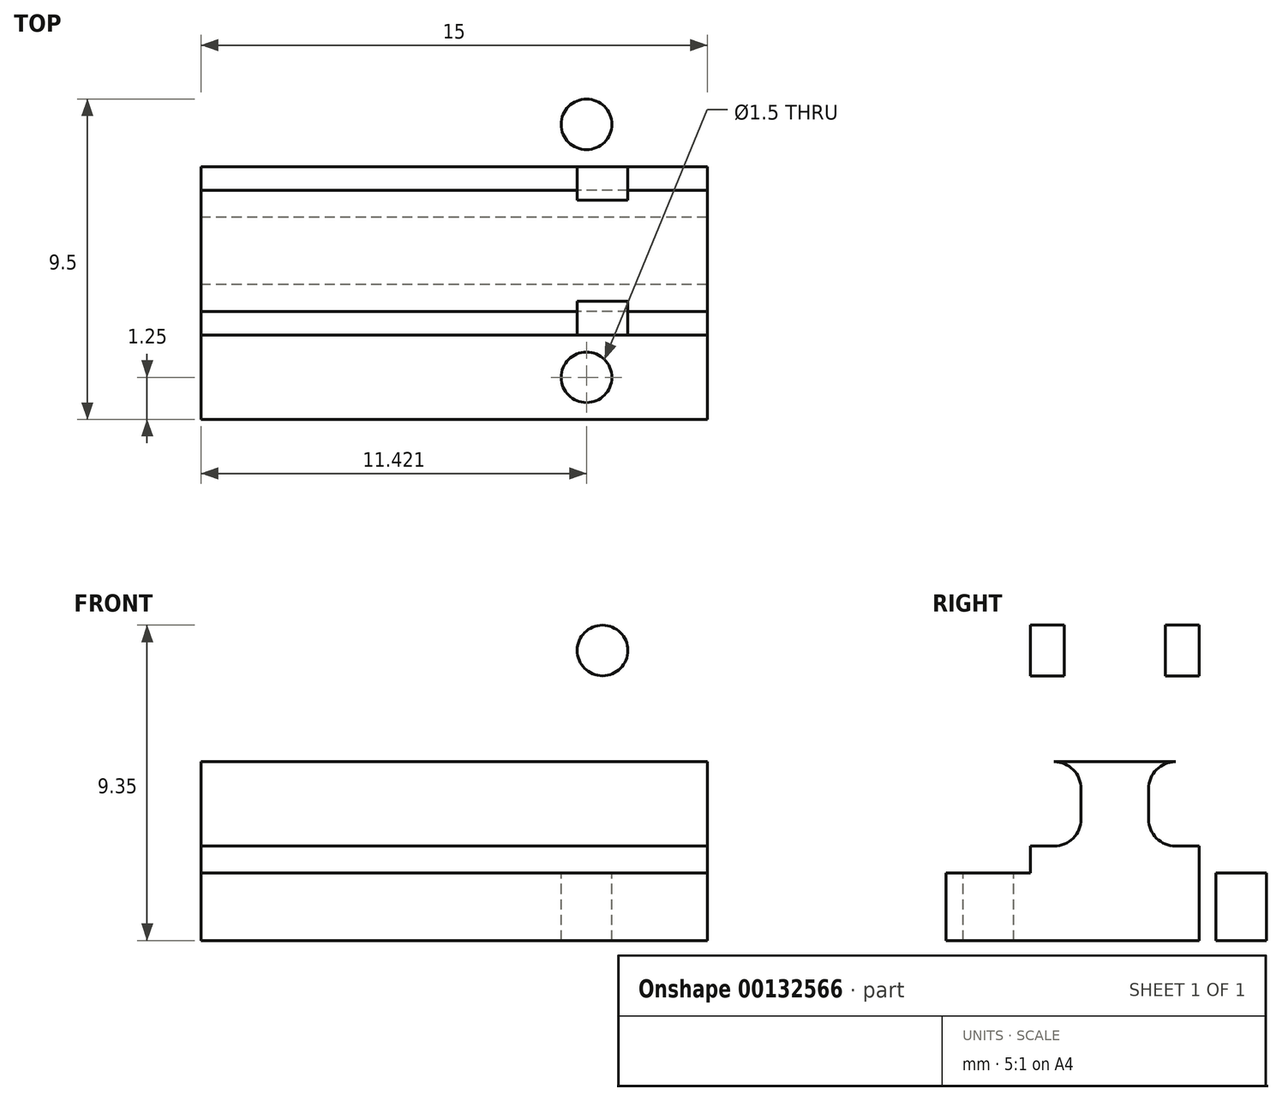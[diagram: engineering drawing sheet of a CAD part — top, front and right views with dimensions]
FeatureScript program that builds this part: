
annotation { "Feature Type Name" : "Feature", "Feature Type Description" : "" }
export const myFeature = defineFeature(function(context is Context, id is Id, definition is map)
    precondition{}
    {
        {
            var Q0;
            Q0=qCreatedBy(makeId("Right.planeOp"),FACE);
            var sketch = newSketch(context, id + "F0", { "sketchPlane" : qUnion([Q0])});
            skLineSegment(sketch, "E0.bottom", {"start": v(-1.5, 2.5) * mm, "end": v(1.5, 2.5) * mm});
            skLineSegment(sketch, "E0.top", {"start": v(-1.5, -2.5) * mm, "end": v(1.5, -2.5) * mm});
            skLineSegment(sketch, "E0.left", {"start": v(-1.5, 2.5) * mm, "end": v(-1.5, -2.5) * mm});
            skLineSegment(sketch, "E0.right", {"start": v(1.5, 2.5) * mm, "end": v(1.5, -2.5) * mm});
            skPoint(sketch, "E0.middle", {"position": v(0, 0) * mm});
            skLineSegment(sketch, "E1.bottom", {"start": v(-2.5, 2.5) * mm, "end": v(2.5, 2.5) * mm});
            skLineSegment(sketch, "E1.left", {"start": v(-2.5, 2.5) * mm, "end": v(-2.5, -7.7) * mm});
            skLineSegment(sketch, "E1.right", {"start": v(2.5, 2.5) * mm, "end": v(2.5, -7.7) * mm});
            skLineSegment(sketch, "E2.bottom", {"start": v(-5, -6.6) * mm, "end": v(5, -6.6) * mm});
            skLineSegment(sketch, "E2.top", {"start": v(-5, -8.6) * mm, "end": v(5, -8.6) * mm});
            skLineSegment(sketch, "E2.left", {"start": v(-5, -6.6) * mm, "end": v(-5, -8.6) * mm});
            skLineSegment(sketch, "E2.right", {"start": v(5, -6.6) * mm, "end": v(5, -8.6) * mm});
            skPoint(sketch, "E2.middle", {"position": v(0, -7.6) * mm});
            skLineSegment(sketch, "E3.bottom", {"start": v(1.8, -3.3) * mm, "end": v(2.5, -3.3) * mm});
            skLineSegment(sketch, "E3.top", {"start": v(1.8, -5.8) * mm, "end": v(2.5, -5.8) * mm});
            skLineSegment(sketch, "E3.left", {"start": v(1, -4.1) * mm, "end": v(1, -5) * mm});
            skLineSegment(sketch, "E3.right", {"start": v(2.5, -3.3) * mm, "end": v(2.5, -5.8) * mm});
            skLineSegment(sketch, "E4.MirrorCS", {"start": v(-1.8, -3.3) * mm, "end": v(-2.5, -3.3) * mm});
            skLineSegment(sketch, "E5.MirrorCS", {"start": v(-1, -4.1) * mm, "end": v(-1, -5) * mm});
            skLineSegment(sketch, "E6.MirrorCS", {"start": v(-1.8, -5.8) * mm, "end": v(-2.5, -5.8) * mm});
            skPoint(sketch, "E7.visualSharp", {"position": v(-1, -3.3) * mm});
            skArc(sketch, "E7.filletArc", {"start": v(-1, -4.1) * mm, "mid": v(-1.23, -3.53) * mm, "end": v(-1.8, -3.3) * mm});
            skPoint(sketch, "E8.visualSharp", {"position": v(-1, -5.8) * mm});
            skArc(sketch, "E8.filletArc", {"start": v(-1.8, -5.8) * mm, "mid": v(-1.23, -5.57) * mm, "end": v(-1, -5) * mm});
            skPoint(sketch, "E9.visualSharp", {"position": v(1, -3.3) * mm});
            skArc(sketch, "E9.filletArc", {"start": v(1.8, -3.3) * mm, "mid": v(1.23, -3.53) * mm, "end": v(1, -4.1) * mm});
            skPoint(sketch, "E10.visualSharp", {"position": v(1, -5.8) * mm});
            skArc(sketch, "E10.filletArc", {"start": v(1, -5) * mm, "mid": v(1.23, -5.57) * mm, "end": v(1.8, -5.8) * mm});
            skSolve(sketch);
        }
        {
            var Q0;
            Q0=makeQuery(id+"F0.imprint","IMPRINT",FACE,{"disambiguationData":[TD([[makeQuery(id+"F0.imprint","IMPRINT",EDGE,{"derivedFrom":sQuery(id+"F0.wireOp",EDGE,"E0.top")}),-1.0]])]});
            var Q1;
            Q1=makeQuery(id+"F0.imprint","IMPRINT",FACE,{"disambiguationData":[TD([[makeQuery(id+"F0.imprint","IMPRINT",EDGE,{"derivedFrom":sQuery(id+"F0.wireOp",EDGE,"E2.top")}),1.0]])]});
            extrude(context, id + "F1", {"entities" : qUnion([Q0, Q1]), "endBound" : BoundingType.SYMMETRIC, "depth" : 15 * mm});
        }
        {
            var Q0;
            {var subQ0=sQuery(id+"F0.wireOp",EDGE,"E1.right");Q0=makeQuery(id+"F1.opExtrude","SWEPT_FACE",FACE,{"disambiguationData":[OSD([subQ0]),TDD([makeQuery(id+"F0.imprint","IMPRINT",EDGE,{"disambiguationData":[TD([[makeQuery(id+"F0.imprint","INTERSECT",VERTEX,{"derivedFrom":[sQuery(id+"F0.wireOp",EDGE,"E1.bottom"),subQ0]}),-1.0]])],"derivedFrom":subQ0})])]});}
            var sketch = newSketch(context, id + "F2", { "sketchPlane" : qUnion([Q0])});
            skCircle(sketch, "E11", {"center": v(4.4, 0) * mm, "radius": 0.75 * mm});
            skCircle(sketch, "E12.MirrorC", {"center": v(-4.4, 0) * mm, "radius": 0.75 * mm});
            skSolve(sketch);
        }
        {
            var Q0;
            Q0=makeQuery(id+"F2.imprint","IMPRINT",FACE,{"disambiguationData":[TD([[makeQuery(id+"F2.imprint","IMPRINT",EDGE,{"derivedFrom":sQuery(id+"F2.wireOp",EDGE,"E12.MirrorC")}),-1.0]])]});
            var Q1;
            Q1=makeQuery(id+"F2.imprint","IMPRINT",FACE,{"disambiguationData":[TD([[makeQuery(id+"F2.imprint","IMPRINT",EDGE,{"derivedFrom":sQuery(id+"F2.wireOp",EDGE,"E11")}),1.0]])]});
            extrude(context, id + "F3", {"entities" : qUnion([Q0, Q1]), "operationType" : NewBodyOperationType.REMOVE, "endBound" : BoundingType.THROUGH_ALL, "oppositeDirection" : true, "depth" : 25 * mm});
        }
        {
            var Q0;
            {var subQ0=sQuery(id+"F0.wireOp",EDGE,"E2.bottom");Q0=makeQuery(id+"F1.opExtrude","SWEPT_FACE",FACE,{"disambiguationData":[OSD([subQ0]),TDD([makeQuery(id+"F0.imprint","IMPRINT",EDGE,{"disambiguationData":[TD([[makeQuery(id+"F0.imprint","INTERSECT",VERTEX,{"derivedFrom":[subQ0,sQuery(id+"F0.wireOp",EDGE,"E2.right")]}),1.0]])],"derivedFrom":subQ0})])]});}
            var sketch = newSketch(context, id + "F4", { "sketchPlane" : qUnion([Q0])});
            skCircle(sketch, "E13", {"center": v(-3.92, 3.75) * mm, "radius": 0.75 * mm});
            skPoint(sketch, "E13.centerSnap0", {"position": v(-7.5, 3.75) * mm});
            skCircle(sketch, "E14.MirrorC", {"center": v(3.92, 3.75) * mm, "radius": 0.75 * mm});
            skCircle(sketch, "E15.MirrorC", {"center": v(3.92, -3.75) * mm, "radius": 0.75 * mm});
            skCircle(sketch, "E16.MirrorC", {"center": v(-3.92, -3.75) * mm, "radius": 0.75 * mm});
            skSolve(sketch);
        }
        {
            var Q0;
            Q0=makeQuery(id+"F4.imprint","IMPRINT",FACE,{"disambiguationData":[TD([[makeQuery(id+"F4.imprint","IMPRINT",EDGE,{"derivedFrom":sQuery(id+"F4.wireOp",EDGE,"E16.MirrorC")}),-1.0]])]});
            var Q1;
            Q1=makeQuery(id+"F4.imprint","IMPRINT",FACE,{"disambiguationData":[TD([[makeQuery(id+"F4.imprint","IMPRINT",EDGE,{"derivedFrom":sQuery(id+"F4.wireOp",EDGE,"E15.MirrorC")}),1.0]])]});
            var Q2;
            Q2=makeQuery(id+"F4.imprint","IMPRINT",FACE,{"disambiguationData":[TD([[makeQuery(id+"F4.imprint","IMPRINT",EDGE,{"derivedFrom":sQuery(id+"F4.wireOp",EDGE,"E14.MirrorC")}),-1.0]])]});
            var Q3;
            Q3=makeQuery(id+"F4.imprint","IMPRINT",FACE,{"disambiguationData":[TD([[makeQuery(id+"F4.imprint","IMPRINT",EDGE,{"derivedFrom":sQuery(id+"F4.wireOp",EDGE,"E13")}),1.0]])]});
            extrude(context, id + "F5", {"entities" : qUnion([Q0, Q1, Q2, Q3]), "operationType" : NewBodyOperationType.REMOVE, "endBound" : BoundingType.THROUGH_ALL, "oppositeDirection" : true, "depth" : 25 * mm});
        }
    });
